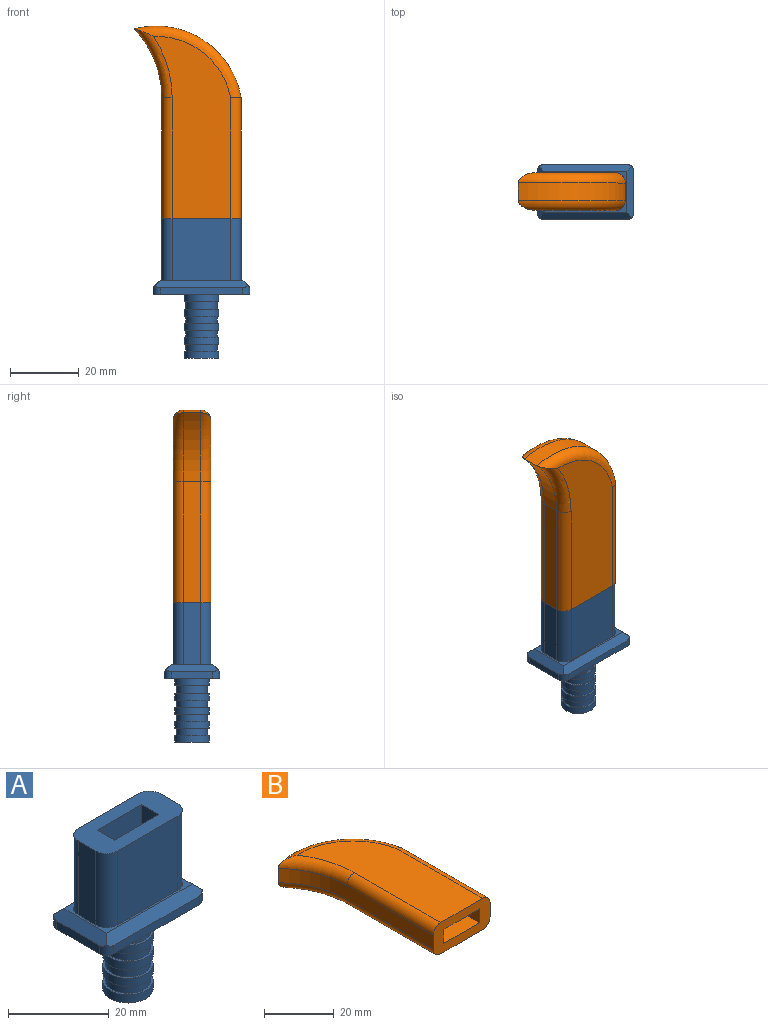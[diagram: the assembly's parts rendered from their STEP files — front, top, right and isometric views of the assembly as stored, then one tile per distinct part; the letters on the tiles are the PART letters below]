
ASSEMBLY  parts=2 mates=1
PART A: 46 faces, bbox 28x16x40.4 mm
  f0: plane 23x11mm, normal (0,0,1), area 184mm2, adj f1,f2,f3,f4,f5,f6,f7,f8
  f1: plane 18x5mm, normal (1,0,0), area 90mm2, adj f0,f2,f8,f19
  f2: cylinder r=3mm len=18mm, axis (0,0,-1), area 84.8mm2, adj f0,f1,f3,f19
  f3: plane 18x17mm, normal (0,1,0), area 306mm2, adj f0,f2,f4,f19
  f4: cylinder r=3mm len=18mm, axis (0,0,-1), area 84.8mm2, adj f0,f3,f5,f19
  f5: plane 18x5mm, normal (-1,0,0), area 90mm2, adj f0,f4,f6,f19
  f6: cylinder r=3mm len=18mm, axis (0,0,-1), area 84.8mm2, adj f0,f5,f7,f19
  f7: plane 18x17mm, normal (0,-1,0), area 306mm2, adj f0,f6,f8,f19
  f8: cylinder r=3mm len=18mm, axis (0,0,-1), area 84.8mm2, adj f0,f1,f7,f19
  f9: plane 17x12.5mm, normal (0,1,0), area 212.5mm2, adj f0,f10,f12,f13
  f10: plane 17x4.9mm, normal (-1,0,0), area 83.3mm2, adj f0,f9,f11,f13
  f11: plane 17x12.5mm, normal (0,-1,0), area 212.5mm2, adj f0,f10,f12,f13
  f12: plane 17x4.9mm, normal (1,0,0), area 83.3mm2, adj f0,f9,f11,f13
  f13: plane 12.5x4.9mm, normal (0,0,1), area 61.2mm2, adj f9,f10,f11,f12
  f14: plane 12x2mm, normal (1,0,0), area 24mm2, adj f18,f23,f24,f27
  f15: plane 24x2mm, normal (0,1,0), area 48mm2, adj f18,f21,f24,f25
  f16: plane 12x2mm, normal (-1,0,0), area 24mm2, adj f18,f20,f25,f26
  f17: plane 24x2mm, normal (0,-1,0), area 48mm2, adj f18,f22,f26,f27
  f18: plane 28x16mm, normal (0,0,-1), area 366mm2, adj f14,f15,f16,f17,f24,f25,f26,f27
  f19: plane 24x12mm, normal (0,0,1), area 42.7mm2, adj f1,f2,f3,f4,f5,f6,f7,f8
  f20: plane 14.83x2mm, normal (-0.71,0,0.71), area 38.4mm2, adj f16,f19,f21,f22,f25,f26
  f21: plane 26.83x2mm, normal (0,0.71,0.71), area 72.3mm2, adj f15,f19,f20,f23,f24,f25
  f22: plane 26.83x2mm, normal (0,-0.71,0.71), area 72.3mm2, adj f17,f19,f20,f23,f26,f27
  f23: plane 14.83x2mm, normal (0.71,0,0.71), area 38.4mm2, adj f14,f19,f21,f22,f24,f27
  f24: cylinder r=2mm len=2.59mm, axis (0,0,-1), area 6.9mm2, adj f14,f15,f18,f21,f23
  f25: cylinder r=2mm len=2.59mm, axis (0,0,1), area 6.9mm2, adj f15,f16,f18,f20,f21
  f26: cylinder r=2mm len=2.59mm, axis (0,0,-1), area 6.9mm2, adj f16,f17,f18,f20,f22
  f27: cylinder r=2mm len=2.59mm, axis (0,0,1), area 6.9mm2, adj f14,f17,f18,f22,f23
  f28: cylinder r=5mm len=10mm, axis (0,0,1), area 62.8mm2, adj f18,f29
  f29: plane 10x10mm, normal (0,0,-1), area 14.9mm2, adj f28,f30
  f30: cylinder r=4.5mm len=9mm, axis (0,0,1), area 68.7mm2, adj f29,f31
  f31: plane 10x10mm, normal (0,0,1), area 14.9mm2, adj f30,f32
  f32: cylinder r=5mm len=10mm, axis (0,0,1), area 62.8mm2, adj f31,f33
  f33: plane 10x10mm, normal (0,0,-1), area 14.9mm2, adj f32,f34
  f34: cylinder r=4.5mm len=9mm, axis (0,0,1), area 56.5mm2, adj f33,f35
  f35: plane 10x10mm, normal (0,0,1), area 14.9mm2, adj f34,f36
  f36: cylinder r=5mm len=10mm, axis (0,0,1), area 62.8mm2, adj f35,f37
  f37: plane 10x10mm, normal (0,0,-1), area 14.9mm2, adj f36,f38
  f38: cylinder r=4.5mm len=9mm, axis (0,0,1), area 56.5mm2, adj f37,f39
  f39: plane 10x10mm, normal (0,0,1), area 14.9mm2, adj f38,f40
  f40: cylinder r=5mm len=10mm, axis (0,0,1), area 62.8mm2, adj f39,f41
  f41: plane 10x10mm, normal (0,0,-1), area 14.9mm2, adj f40,f42
  f42: cylinder r=4.5mm len=9mm, axis (0,0,1), area 56.5mm2, adj f41,f43
  f43: plane 10x10mm, normal (0,0,1), area 14.9mm2, adj f42,f44
  f44: cylinder r=5mm len=10mm, axis (0,0,1), area 62.8mm2, adj f43,f45
  f45: plane 10x10mm, normal (0,0,-1), area 78.5mm2, adj f44
PART B: 22 faces, bbox 33.6x60.5x11 mm
  f0: plane 3.05x3mm, normal (0,1,0), area 0mm2, adj f6,f8,f19
  f1: plane 3.05x3mm, normal (0,1,0), area 0mm2, adj f5,f10,f21
  f2: plane 23x11mm, normal (0,-1,0), area 174.2mm2, adj f3,f4,f5,f6,f7,f8,f9,f10
  f3: plane 35x5mm, normal (1,0,0), area 175mm2, adj f2,f8,f10,f16
  f4: plane 35x5mm, normal (-1,0,0), area 175mm2, adj f2,f7,f9,f17
  f5: plane 52.82x22.41mm, normal (0,0,1), area 831.9mm2, adj f1,f2,f9,f10,f20,f21
  f6: plane 52.82x22.41mm, normal (0,0,-1), area 831.9mm2, adj f0,f2,f7,f8,f18,f19
  f7: cylinder r=3mm len=35mm, axis (0,-1,0), area 164.9mm2, adj f2,f4,f6,f18
  f8: cylinder r=3mm len=35mm, axis (0,1,0), area 164.9mm2, adj f0,f2,f3,f6
  f9: cylinder r=3mm len=35mm, axis (0,1,0), area 164.9mm2, adj f2,f4,f5,f20
  f10: cylinder r=3mm len=35mm, axis (0,-1,0), area 164.9mm2, adj f1,f2,f3,f5
  f11: plane 35x14.5mm, normal (0,0,1), area 507.5mm2, adj f2,f12,f14,f15
  f12: plane 35x4.9mm, normal (-1,0,0), area 171.5mm2, adj f2,f11,f13,f15
  f13: plane 35x14.5mm, normal (0,0,-1), area 507.5mm2, adj f2,f12,f14,f15
  f14: plane 35x4.9mm, normal (1,0,0), area 171.5mm2, adj f2,f11,f13,f15
  f15: plane 14.5x4.9mm, normal (0,-1,0), area 71mm2, adj f11,f12,f13,f14
  f16: cylinder r=25mm len=31mm, axis (0,0,-1), area 207.5mm2, adj f3,f17,f19,f21
  f17: cylinder r=29mm len=20mm, axis (0,0,-1), area 110.3mm2, adj f4,f16,f18,f20
  f18: torus R=32mm, axis (0,0,1), area 98.8mm2, adj f6,f7,f17,f19
  f19: torus R=22mm, axis (0,0,1), area 177.6mm2, adj f0,f6,f16,f18
  f20: torus R=32mm, axis (0,0,1), area 98.8mm2, adj f5,f9,f17,f21
  f21: torus R=22mm, axis (0,0,1), area 177.6mm2, adj f1,f5,f16,f20
PLACE A t=(0.11,0.07,2.22)mm
PLACE B rot(axis=(1,0,0),90deg) t=(0.11,5.57,37.72)mm
MATE fastened B.f2 <-> A.f28  axis (0,0,-1) through (0.11,0.07,20.22)mm
